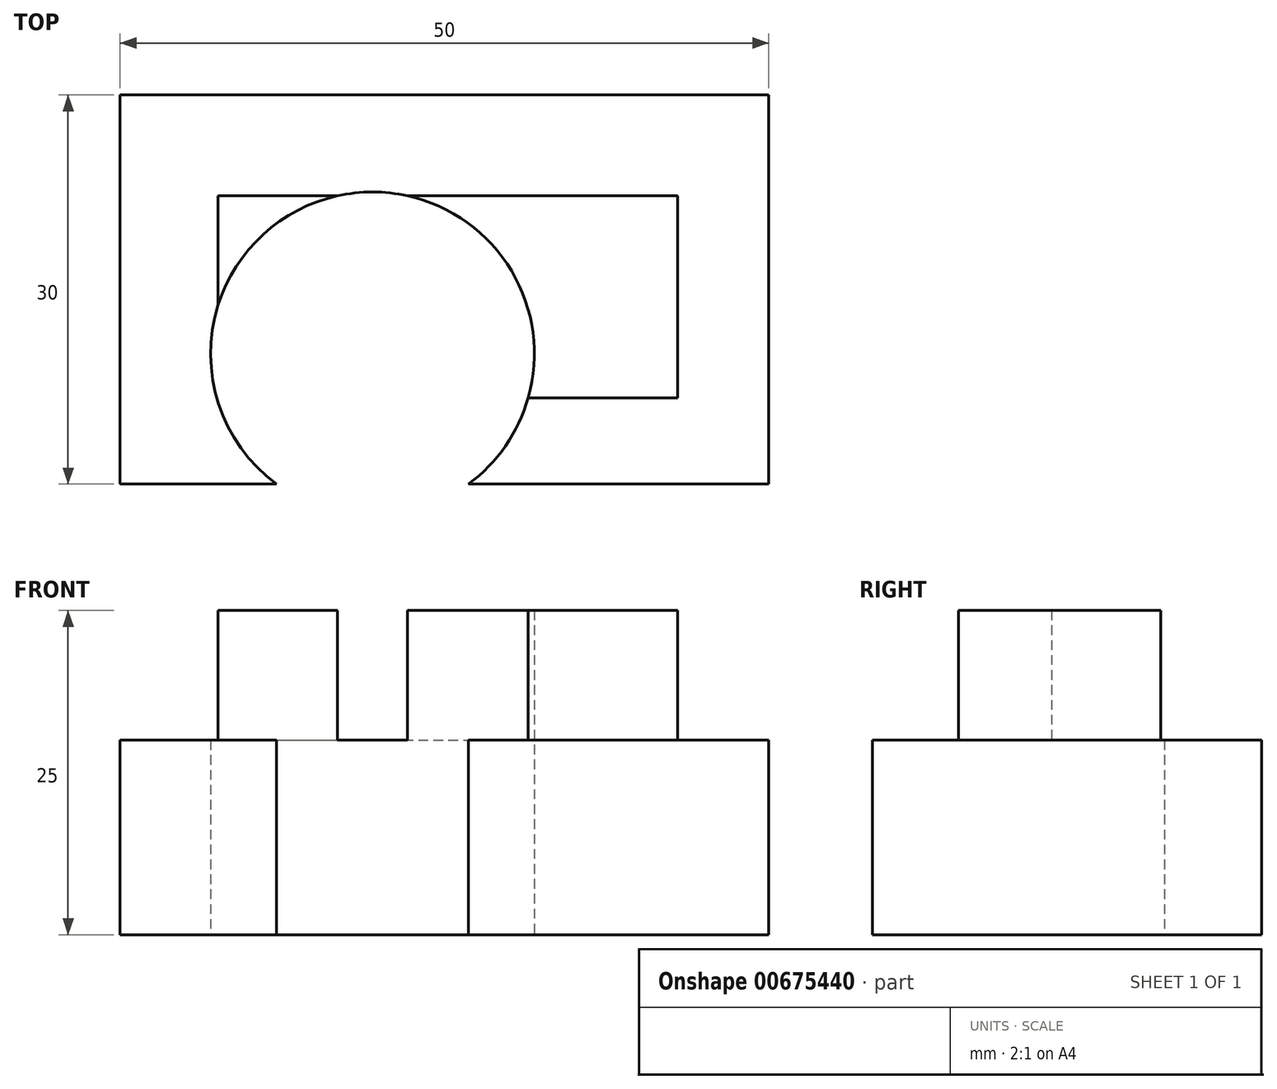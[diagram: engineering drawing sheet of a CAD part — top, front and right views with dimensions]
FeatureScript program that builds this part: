
annotation { "Feature Type Name" : "Feature", "Feature Type Description" : "" }
export const myFeature = defineFeature(function(context is Context, id is Id, definition is map)
    precondition{}
    {
        {
            var Q0;
            Q0=qCreatedBy(makeId("Top.planeOp"),FACE);
            var sketch = newSketch(context, id + "F0", { "sketchPlane" : qUnion([Q0])});
            skLineSegment(sketch, "E0.bottom", {"start": v(-59.54, 37.38) * mm, "end": v(-9.54, 37.38) * mm});
            skLineSegment(sketch, "E0.top", {"start": v(-59.54, 7.38) * mm, "end": v(-9.54, 7.38) * mm});
            skLineSegment(sketch, "E0.left", {"start": v(-59.54, 37.38) * mm, "end": v(-59.54, 7.38) * mm});
            skLineSegment(sketch, "E0.right", {"start": v(-9.54, 37.38) * mm, "end": v(-9.54, 7.38) * mm});
            skSolve(sketch);
        }
        {
            var Q0;
            Q0 = qSketchRegion(id + "F0", true);
            extrude(context, id + "F1", {"entities" : qUnion([Q0]), "depth" : 15 * mm, "offsetDistance" : 25 * mm});
        }
        {
            var Q0;
            Q0=makeQuery(id+"F1.opExtrude","CAP_FACE",FACE,{"disambiguationData":[OSD([sQuery(id+"F0.wireOp",EDGE,"E0.bottom"),sQuery(id+"F0.wireOp",EDGE,"E0.top"),sQuery(id+"F0.wireOp",EDGE,"E0.left"),sQuery(id+"F0.wireOp",EDGE,"E0.right")])],"isStart":false});
            var sketch = newSketch(context, id + "F2", { "sketchPlane" : qUnion([Q0])});
            skLineSegment(sketch, "E1.bottom", {"start": v(-51.98, 29.6) * mm, "end": v(-16.57, 29.6) * mm});
            skLineSegment(sketch, "E1.top", {"start": v(-51.98, 14.02) * mm, "end": v(-16.57, 14.02) * mm});
            skLineSegment(sketch, "E1.left", {"start": v(-51.98, 29.6) * mm, "end": v(-51.98, 14.02) * mm});
            skLineSegment(sketch, "E1.right", {"start": v(-16.57, 29.6) * mm, "end": v(-16.57, 14.02) * mm});
            skSolve(sketch);
        }
        {
            var Q0;
            Q0=makeQuery(id+"F2.imprint","IMPRINT",FACE,{"disambiguationData":[TD([[makeQuery(id+"F2.imprint","IMPRINT",EDGE,{"derivedFrom":sQuery(id+"F2.wireOp",EDGE,"E1.bottom")}),-1.0]])]});
            var Q1;
            Q1 = qSketchRegion(id + "F2", true);
            extrude(context, id + "F3", {"entities" : qUnion([Q0, Q1]), "operationType" : NewBodyOperationType.ADD, "depth" : 10 * mm, "offsetDistance" : 25 * mm});
        }
        {
            var Q0;
            Q0=qCreatedBy(makeId("Top.planeOp"),FACE);
            var sketch = newSketch(context, id + "F4", { "sketchPlane" : qUnion([Q0])});
            skCircle(sketch, "E2", {"center": v(-40.08, 17.42) * mm, "radius": 12.48 * mm});
            skSolve(sketch);
        }
        {
            var Q0;
            Q0 = qSketchRegion(id + "F4", true);
            extrude(context, id + "F5", {"entities" : qUnion([Q0]), "operationType" : NewBodyOperationType.REMOVE, "depth" : 25 * mm, "offsetDistance" : 25 * mm});
        }
    });
